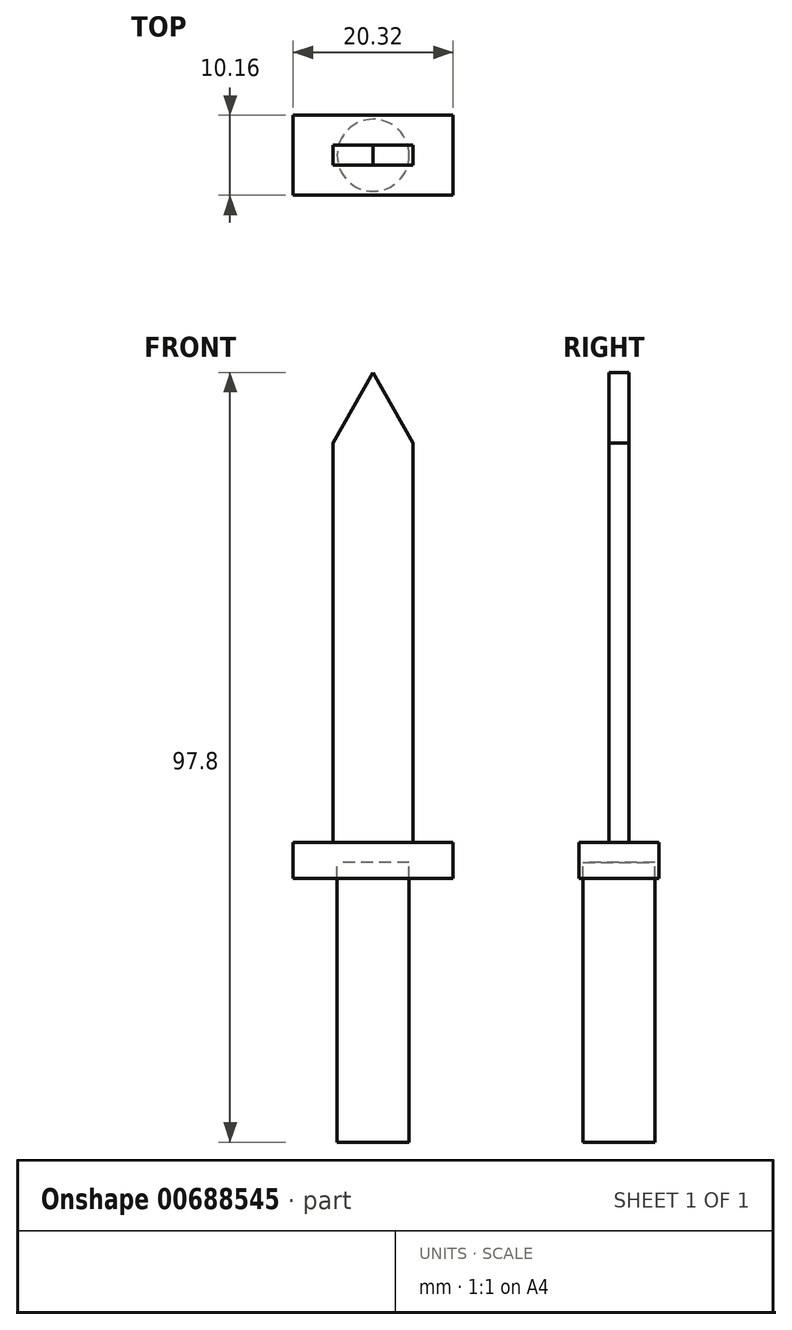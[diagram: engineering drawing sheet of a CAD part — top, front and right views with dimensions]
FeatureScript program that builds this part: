
annotation { "Feature Type Name" : "Feature", "Feature Type Description" : "" }
export const myFeature = defineFeature(function(context is Context, id is Id, definition is map)
    precondition{}
    {
        {
            var Q0;
            Q0=qCreatedBy(makeId("Front.planeOp"),FACE);
            var sketch = newSketch(context, id + "F0", { "sketchPlane" : qUnion([Q0])});
            skLineSegment(sketch, "E0.bottom", {"start": v(0, 15.8) * mm, "end": v(-4.57, 15.8) * mm});
            skLineSegment(sketch, "E0.top", {"start": v(0, -19.75) * mm, "end": v(-4.57, -19.75) * mm});
            skLineSegment(sketch, "E0.left", {"start": v(0, 15.8) * mm, "end": v(0, -19.75) * mm});
            skLineSegment(sketch, "E0.right", {"start": v(-4.57, 15.8) * mm, "end": v(-4.57, -19.75) * mm});
            skSolve(sketch);
        }
        {
            var Q0;
            Q0 = qSketchRegion(id + "F0", true);
            var Q1;
            Q1=sQuery(id+"F0.wireOp",EDGE,"E0.left");
            revolve(context, id + "F1", {"entities" : qUnion([Q0]), "axis" : qUnion([Q1]), "revolveType" : RevolveType.FULL});
        }
        {
            var Q0;
            Q0=qCreatedBy(makeId("Top.planeOp"),FACE);
            cPlane(context, id + "F2", {"entities" : qUnion([Q0]), "cplaneType" : CPlaneType.OFFSET, "offset" : 18.34 * mm, "width" : 152.4 * mm, "height" : 152.4 * mm});
        }
        {
            var Q0;
            Q0=qCreatedBy(id+"F2.planeOp",FACE);
            var sketch = newSketch(context, id + "F3", { "sketchPlane" : qUnion([Q0])});
            skLineSegment(sketch, "E1", {"start": v(0, 0) * mm, "end": v(-10.16, 0) * mm});
            skLineSegment(sketch, "E2", {"start": v(-10.16, 0) * mm, "end": v(-10.16, -5.08) * mm});
            skLineSegment(sketch, "E3", {"start": v(-10.16, -5.08) * mm, "end": v(0, -5.08) * mm});
            skLineSegment(sketch, "E4", {"start": v(0, -5.08) * mm, "end": v(0, 0) * mm});
            skLineSegment(sketch, "E5.MirrorCS", {"start": v(-10.16, 5.08) * mm, "end": v(0, 5.08) * mm});
            skLineSegment(sketch, "E6.MirrorCS", {"start": v(0, 5.08) * mm, "end": v(0, 0) * mm});
            skLineSegment(sketch, "E7.MirrorCS", {"start": v(-10.16, 0) * mm, "end": v(-10.16, 5.08) * mm});
            skLineSegment(sketch, "E8.MirrorCS", {"start": v(0, 0) * mm, "end": v(10.16, 0) * mm});
            skLineSegment(sketch, "E9.MirrorCS", {"start": v(10.16, 0) * mm, "end": v(10.16, 5.08) * mm});
            skLineSegment(sketch, "E10.MirrorCS", {"start": v(10.16, -5.08) * mm, "end": v(0, -5.08) * mm});
            skLineSegment(sketch, "E11.MirrorCS", {"start": v(10.16, 5.08) * mm, "end": v(0, 5.08) * mm});
            skLineSegment(sketch, "E12.MirrorCS", {"start": v(10.16, 0) * mm, "end": v(10.16, -5.08) * mm});
            skSolve(sketch);
        }
        {
            var Q0;
            Q0 = qSketchRegion(id + "F3", true);
            extrude(context, id + "F4", {"entities" : qUnion([Q0]), "oppositeDirection" : true, "depth" : 4.57 * mm, "offsetDistance" : 25.4 * mm});
        }
        {
            var Q0;
            Q0=qCreatedBy(makeId("Front.planeOp"),FACE);
            var sketch = newSketch(context, id + "F5", { "sketchPlane" : qUnion([Q0])});
            skLineSegment(sketch, "E13", {"start": v(0, 18.3) * mm, "end": v(-5.08, 18.3) * mm});
            skLineSegment(sketch, "E14", {"start": v(-5.08, 18.3) * mm, "end": v(-5.08, 69.1) * mm});
            skLineSegment(sketch, "E15", {"start": v(-5.08, 69.1) * mm, "end": v(0, 78.05) * mm});
            skLineSegment(sketch, "E16.MirrorCS", {"start": v(5.08, 18.3) * mm, "end": v(5.08, 69.1) * mm});
            skLineSegment(sketch, "E17.MirrorCS", {"start": v(5.08, 69.1) * mm, "end": v(0, 78.05) * mm});
            skLineSegment(sketch, "E18.MirrorCS", {"start": v(0, 18.3) * mm, "end": v(5.08, 18.3) * mm});
            skSolve(sketch);
        }
        {
            var Q0;
            Q0 = qSketchRegion(id + "F5", true);
            extrude(context, id + "F6", {"entities" : qUnion([Q0]), "operationType" : NewBodyOperationType.ADD, "oppositeDirection" : true, "depth" : 1.27 * mm, "offsetDistance" : 25.4 * mm});
        }
        {
            var Q0;
            Q0 = qSketchRegion(id + "F5", true);
            extrude(context, id + "F7", {"entities" : qUnion([Q0]), "operationType" : NewBodyOperationType.ADD, "depth" : 1.27 * mm, "offsetDistance" : 25.4 * mm});
        }
    });
